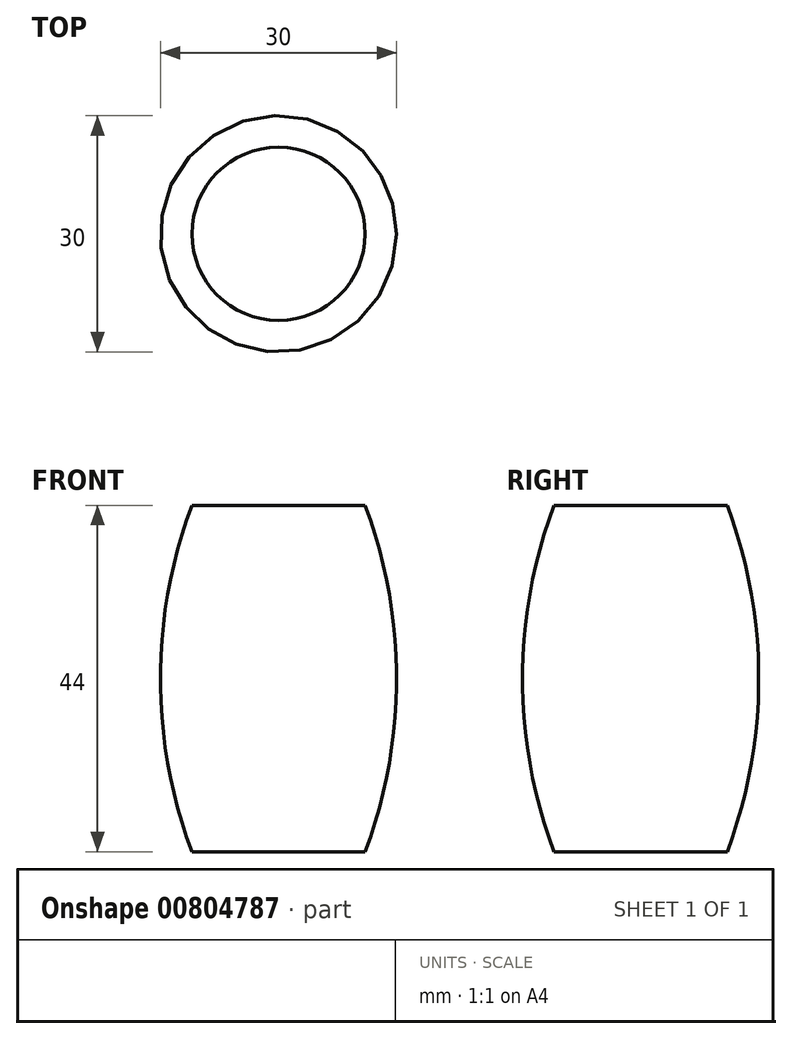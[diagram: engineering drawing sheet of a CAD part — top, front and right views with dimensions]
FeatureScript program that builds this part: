
annotation { "Feature Type Name" : "Feature", "Feature Type Description" : "" }
export const myFeature = defineFeature(function(context is Context, id is Id, definition is map)
    precondition{}
    {
        {
            var Q0;
            Q0=qCreatedBy(makeId("Top.planeOp"),FACE);
            var sketch = newSketch(context, id + "F0", { "sketchPlane" : qUnion([Q0])});
            skCircle(sketch, "E0", {"center": v(0, 0) * mm, "radius": 11 * mm});
            skSolve(sketch);
        }
        {
            var Q0;
            Q0=qCreatedBy(makeId("Top.planeOp"),FACE);
            cPlane(context, id + "F1", {"entities" : qUnion([Q0]), "cplaneType" : CPlaneType.OFFSET, "offset" : 44 * mm, "oppositeDirection" : true, "width" : 150 * mm, "height" : 150 * mm});
        }
        {
            var Q0;
            Q0=qCreatedBy(id+"F1.planeOp",FACE);
            var sketch = newSketch(context, id + "F2", { "sketchPlane" : qUnion([Q0])});
            skCircle(sketch, "E1", {"center": v(0, 0) * mm, "radius": 11 * mm});
            skSolve(sketch);
        }
        {
            var Q0;
            Q0=qCreatedBy(id+"F1.planeOp",FACE);
            cPlane(context, id + "F3", {"entities" : qUnion([Q0]), "cplaneType" : CPlaneType.OFFSET, "offset" : 22 * mm, "width" : 150 * mm, "height" : 150 * mm});
        }
        {
            var Q0;
            Q0=qCreatedBy(id+"F3.planeOp",FACE);
            var sketch = newSketch(context, id + "F4", { "sketchPlane" : qUnion([Q0])});
            skCircle(sketch, "E2", {"center": v(0, 0) * mm, "radius": 15 * mm});
            skSolve(sketch);
        }
        {
            var Q0;
            Q0=qCreatedBy(makeId("Front.planeOp"),FACE);
            var sketch = newSketch(context, id + "F5", { "sketchPlane" : qUnion([Q0])});
            skLineSegment(sketch, "E3.0", {"start": v(-11, 0) * mm, "end": v(11, 0) * mm});
            skLineSegment(sketch, "E4.0", {"start": v(-15, -22) * mm, "end": v(15, -22) * mm});
            skLineSegment(sketch, "E5.0", {"start": v(-11, -44) * mm, "end": v(11, -44) * mm});
            skLineSegment(sketch, "E6", {"start": v(0, 0) * mm, "end": v(0, -44) * mm});
            skArc(sketch, "E7", {"start": v(11, -44) * mm, "mid": v(15, -22) * mm, "end": v(11, 0) * mm});
            skSolve(sketch);
        }
        {
            var Q0;
            {var subQ0=sQuery(id+"F5.wireOp",EDGE,"E7");var subQ1=sQuery(id+"F5.wireOp",EDGE,"E3.0");var subQ2=makeQuery(id+"F5.imprint","INTERSECT",VERTEX,{"derivedFrom":[subQ1,subQ0]});Q0=makeQuery(id+"F5.imprint","IMPRINT",FACE,{"disambiguationData":[TD([[makeQuery(id+"F5.imprint","IMPRINT",EDGE,{"disambiguationData":[TD([[subQ2,1.0]])],"derivedFrom":subQ1}),-1.0]])]});}
            var Q1;
            {var subQ0=sQuery(id+"F5.wireOp",EDGE,"E7");var subQ1=sQuery(id+"F5.wireOp",EDGE,"E4.0");var subQ2=makeQuery(id+"F5.imprint","INTERSECT",VERTEX,{"derivedFrom":[subQ1,subQ0]});Q1=makeQuery(id+"F5.imprint","IMPRINT",FACE,{"disambiguationData":[TD([[makeQuery(id+"F5.imprint","IMPRINT",EDGE,{"disambiguationData":[TD([[subQ2,1.0]])],"derivedFrom":subQ1}),-1.0]])]});}
            var Q2;
            Q2=sQuery(id+"F5.wireOp",EDGE,"E7");
            var Q3;
            Q3=sQuery(id+"F5.wireOp",EDGE,"E6");
            revolve(context, id + "F6", {"surfaceOperationType" : NewSurfaceOperationType.NEW, "entities" : qUnion([Q0, Q1]), "surfaceEntities" : qUnion([Q2]), "axis" : qUnion([Q3]), "revolveType" : RevolveType.FULL});
        }
    });
